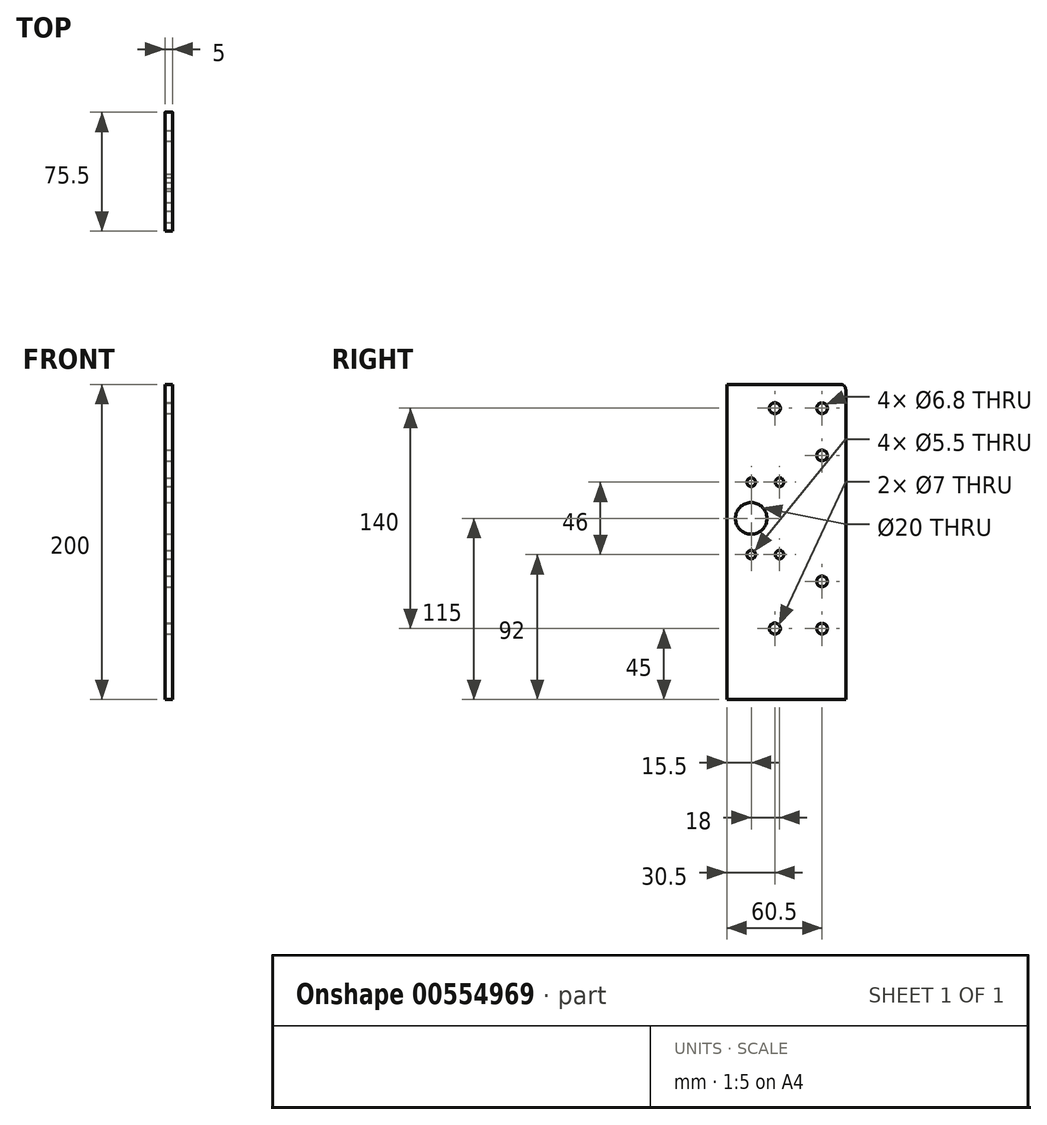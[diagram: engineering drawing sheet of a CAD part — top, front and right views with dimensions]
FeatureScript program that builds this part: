
annotation { "Feature Type Name" : "Feature", "Feature Type Description" : "" }
export const myFeature = defineFeature(function(context is Context, id is Id, definition is map)
    precondition{}
    {
        {
            var Q0;
            Q0=qCreatedBy(makeId("Right.planeOp"),FACE);
            var sketch = newSketch(context, id + "F0", { "sketchPlane" : qUnion([Q0])});
            skLineSegment(sketch, "E0.bottom", {"start": v(37.75, 100) * mm, "end": v(-37.75, 100) * mm});
            skLineSegment(sketch, "E0.top", {"start": v(37.75, -100) * mm, "end": v(-37.75, -100) * mm});
            skLineSegment(sketch, "E0.left", {"start": v(37.75, 100) * mm, "end": v(37.75, -100) * mm});
            skLineSegment(sketch, "E0.right", {"start": v(-37.75, 100) * mm, "end": v(-37.75, -100) * mm});
            skPoint(sketch, "E0.middle", {"position": v(0, 0) * mm});
            skSolve(sketch);
        }
        {
            var Q0;
            Q0 = qSketchRegion(id + "F0", true);
            extrude(context, id + "F1", {"entities" : qUnion([Q0]), "endBound" : BoundingType.SYMMETRIC, "depth" : 5 * mm, "offsetDistance" : 25 * mm});
        }
        {
            var Q0;
            Q0=makeQuery(id+"F1.opExtrude","CAP_FACE",FACE,{"disambiguationData":[OSD([sQuery(id+"F0.wireOp",EDGE,"E0.bottom"),sQuery(id+"F0.wireOp",EDGE,"E0.top"),sQuery(id+"F0.wireOp",EDGE,"E0.left"),sQuery(id+"F0.wireOp",EDGE,"E0.right")])],"isStart":false});
            var sketch = newSketch(context, id + "F2", { "sketchPlane" : qUnion([Q0])});
            skCircle(sketch, "E1", {"center": v(22.75, 85) * mm, "radius": 3.4 * mm});
            skCircle(sketch, "E2", {"center": v(22.75, 55) * mm, "radius": 3.4 * mm});
            skCircle(sketch, "E3", {"center": v(22.75, -55) * mm, "radius": 3.4 * mm});
            skCircle(sketch, "E4", {"center": v(22.75, -25) * mm, "radius": 3.4 * mm});
            skCircle(sketch, "E5", {"center": v(-7.25, 85) * mm, "radius": 3.5 * mm});
            skCircle(sketch, "E6", {"center": v(-7.25, -55) * mm, "radius": 3.5 * mm});
            skCircle(sketch, "E7", {"center": v(-22.25, 15) * mm, "radius": 10 * mm});
            skPoint(sketch, "E8.center.orphan", {"position": v(-7.25, 55) * mm});
            skPoint(sketch, "E9.center.orphan", {"position": v(-7.25, -25) * mm});
            skCircle(sketch, "E10", {"center": v(-22.25, 38) * mm, "radius": 2.75 * mm});
            skCircle(sketch, "E11", {"center": v(-4.25, 38) * mm, "radius": 2.75 * mm});
            skCircle(sketch, "E12", {"center": v(-22.25, -8) * mm, "radius": 2.75 * mm});
            skCircle(sketch, "E13", {"center": v(-4.25, -8) * mm, "radius": 2.75 * mm});
            skSolve(sketch);
        }
        {
            var Q0;
            Q0 = qSketchRegion(id + "F2", true);
            extrude(context, id + "F3", {"entities" : qUnion([Q0]), "operationType" : NewBodyOperationType.REMOVE, "oppositeDirection" : true, "depth" : 5 * mm, "offsetDistance" : 25 * mm});
        }
        {
            var Q0;
            Q0=makeQuery(id+"F1.opExtrude","SWEPT_EDGE",EDGE,{"disambiguationData":[OSD([sQuery(id+"F0.wireOp",EDGE,"E0.bottom"),sQuery(id+"F0.wireOp",EDGE,"E0.left")])]});
            fillet(context, id + "F4", {"entities" : qUnion([Q0]), "radius" : 3 * mm, "tangentPropagation" : true, "allowEdgeOverflow" : false});
        }
    });
